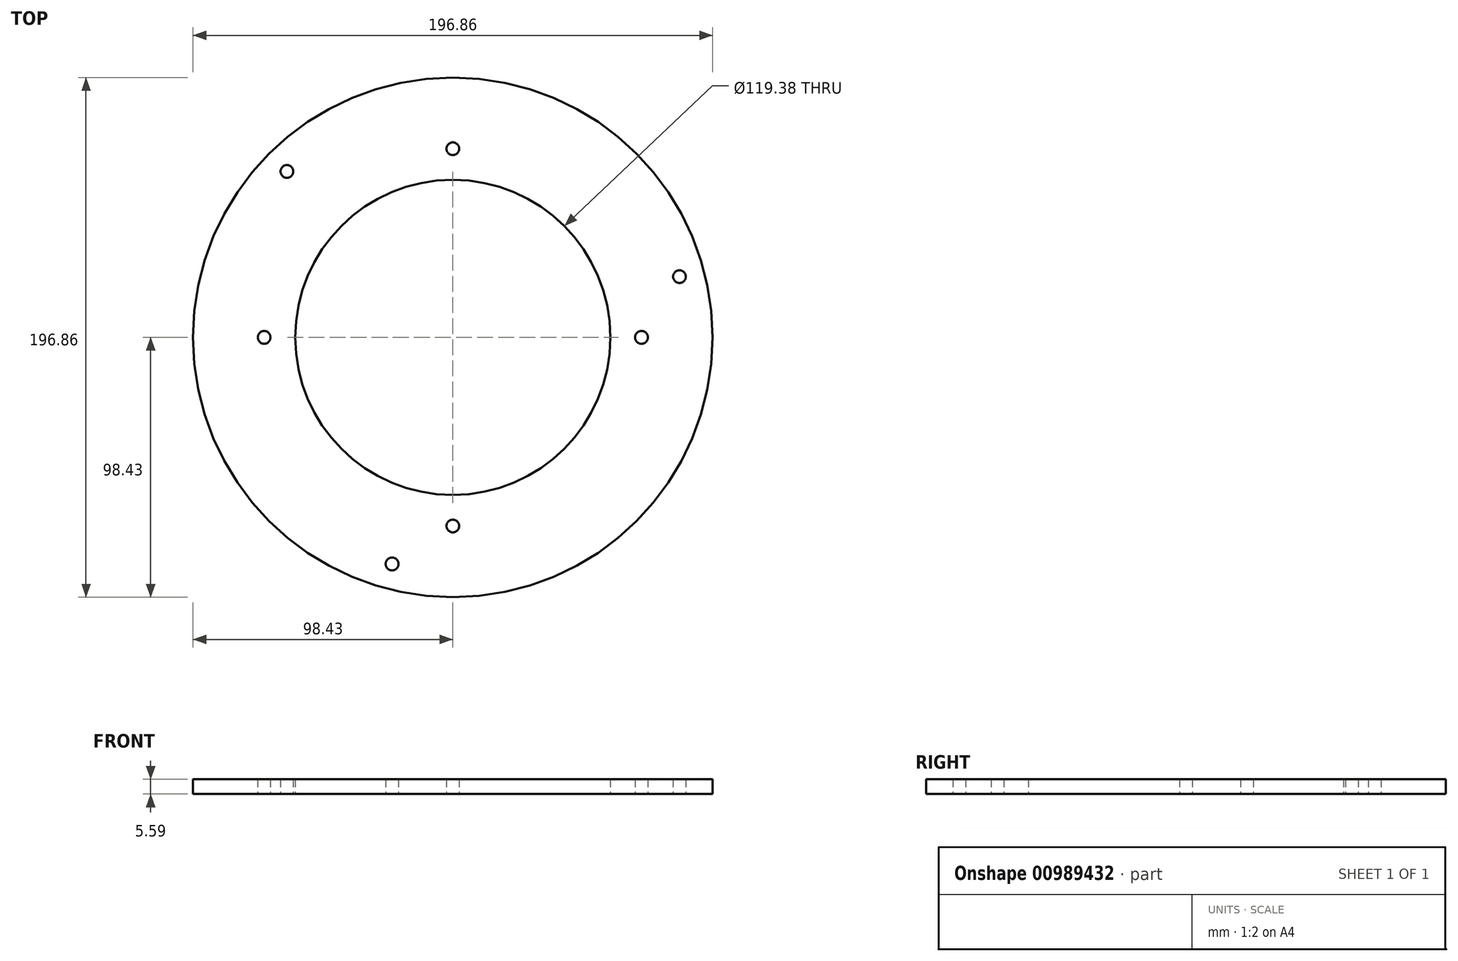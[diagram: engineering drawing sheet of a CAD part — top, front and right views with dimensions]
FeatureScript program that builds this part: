
annotation { "Feature Type Name" : "Feature", "Feature Type Description" : "" }
export const myFeature = defineFeature(function(context is Context, id is Id, definition is map)
    precondition{}
    {
        {
            var Q0;
            Q0=qCreatedBy(makeId("Top.planeOp"),FACE);
            var sketch = newSketch(context, id + "F0", { "sketchPlane" : qUnion([Q0])});
            skCircle(sketch, "E0", {"center": v(0, 0) * mm, "radius": 59.7 * mm});
            skCircle(sketch, "E1", {"center": v(0, 0) * mm, "radius": 71.46 * mm, "construction": true});
            skCircle(sketch, "E2.cCircle", {"center": v(0, 0) * mm, "radius": 50.53 * mm, "construction": true});
            skLineSegment(sketch, "E2.0", {"start": v(0, 71.46) * mm, "end": v(71.46, 0) * mm, "construction": true});
            skLineSegment(sketch, "E2.1", {"start": v(71.46, 0) * mm, "end": v(0, -71.46) * mm, "construction": true});
            skLineSegment(sketch, "E2.2", {"start": v(0, -71.46) * mm, "end": v(-71.46, 0) * mm, "construction": true});
            skLineSegment(sketch, "E2.3", {"start": v(-71.46, 0) * mm, "end": v(0, 71.46) * mm, "construction": true});
            skPoint(sketch, "E2.0.midPoint", {"position": v(35.73, 35.73) * mm});
            skCircle(sketch, "E3", {"center": v(0, 71.46) * mm, "radius": 2.41 * mm});
            skCircle(sketch, "E4", {"center": v(-71.46, 0) * mm, "radius": 2.41 * mm});
            skCircle(sketch, "E5", {"center": v(0, -71.46) * mm, "radius": 2.41 * mm});
            skCircle(sketch, "E6", {"center": v(71.46, 0) * mm, "radius": 2.41 * mm});
            skCircle(sketch, "E7", {"center": v(0, 0) * mm, "radius": 88.9 * mm, "construction": true});
            skCircle(sketch, "E8.cCircle", {"center": v(0, 0) * mm, "radius": 44.45 * mm, "construction": true});
            skLineSegment(sketch, "E8.0", {"start": v(-23, -85.87) * mm, "end": v(-62.86, 62.86) * mm, "construction": true});
            skLineSegment(sketch, "E8.1", {"start": v(-62.86, 62.86) * mm, "end": v(85.87, 23) * mm, "construction": true});
            skLineSegment(sketch, "E8.2", {"start": v(85.87, 23) * mm, "end": v(-23, -85.87) * mm, "construction": true});
            skPoint(sketch, "E8.0.midPoint", {"position": v(-42.94, -11.5) * mm});
            skCircle(sketch, "E9", {"center": v(-23, -85.87) * mm, "radius": 2.41 * mm});
            skCircle(sketch, "E10", {"center": v(-62.86, 62.86) * mm, "radius": 2.41 * mm});
            skCircle(sketch, "E11", {"center": v(85.87, 23) * mm, "radius": 2.41 * mm});
            skLineSegment(sketch, "E12", {"start": v(-35.73, 35.73) * mm, "end": v(-62.86, 62.86) * mm, "construction": true});
            skCircle(sketch, "E13", {"center": v(0, 0) * mm, "radius": 98.43 * mm});
            skSolve(sketch);
        }
        {
            var Q0;
            Q0=makeQuery(id+"F0.imprint","IMPRINT",FACE,{"disambiguationData":[TD([[makeQuery(id+"F0.imprint","IMPRINT",EDGE,{"derivedFrom":sQuery(id+"F0.wireOp",EDGE,"E0")}),-1.0]])]});
            extrude(context, id + "F1", {"entities" : qUnion([Q0]), "depth" : 5.6 * mm, "offsetDistance" : 25.4 * mm});
        }
    });
